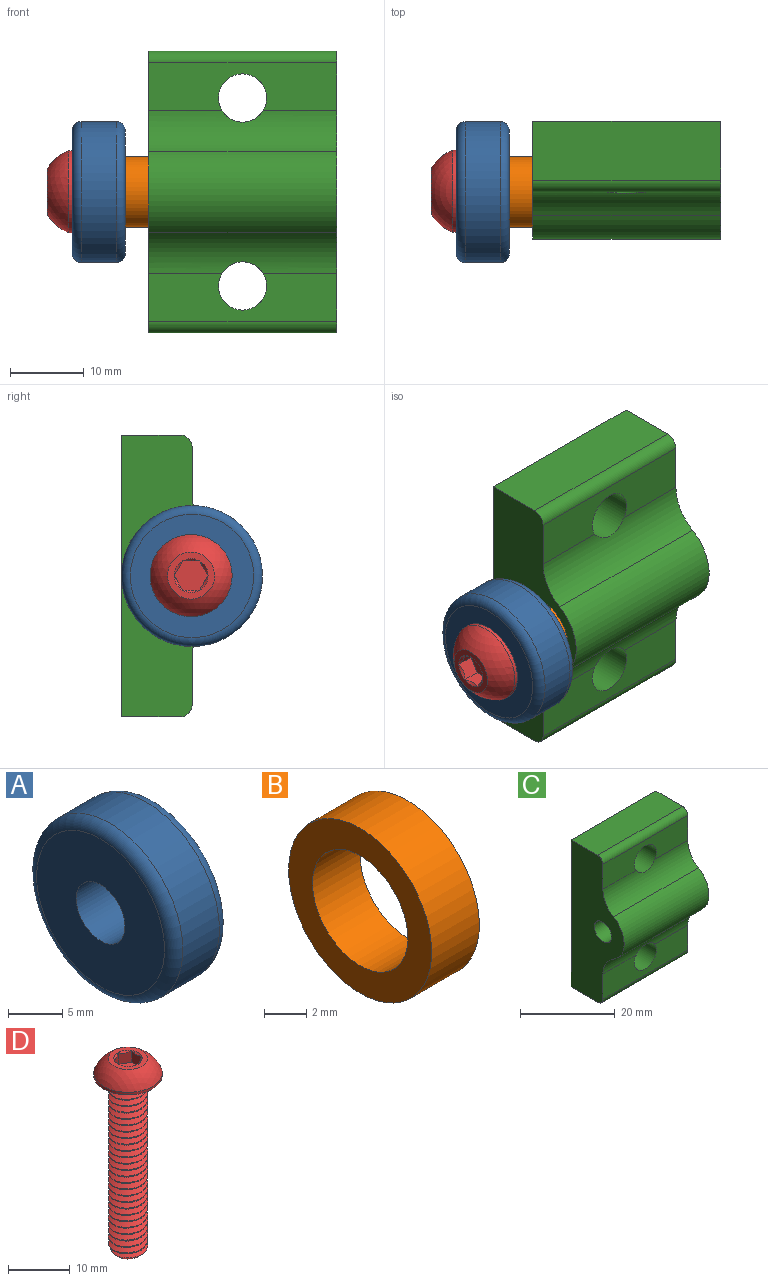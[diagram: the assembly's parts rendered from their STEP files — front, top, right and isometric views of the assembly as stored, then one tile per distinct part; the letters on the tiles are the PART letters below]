
ASSEMBLY  parts=4 mates=3
PART A: 6 faces, bbox 7.1x20.6x20.6 mm
  f0: cylinder r=3.17mm len=7.14mm, axis (-1,0,0), area 142.5mm2, adj f2,f3
  f1: cylinder r=9.53mm len=19.05mm, axis (-1,0,0), area 284.9mm2, adj f4,f5
  f2: plane 16.67x16.67mm, normal (1,0,0), area 186.6mm2, adj f0,f5
  f3: plane 16.67x16.67mm, normal (-1,0,0), area 186.6mm2, adj f0,f4
  f4: torus R=8.33mm, axis (1,0,0), area 106.8mm2, adj f1,f3
  f5: torus R=8.33mm, axis (1,0,0), area 106.8mm2, adj f1,f2
PART B: 4 faces, bbox 3.2x9.5x9.5 mm
  f0: cylinder r=3.17mm len=6.35mm, axis (-1,0,0), area 63.3mm2, adj f2,f3
  f1: cylinder r=4.76mm len=9.53mm, axis (-1,0,0), area 95mm2, adj f2,f3
  f2: plane 9.53x9.53mm, normal (1,0,0), area 39.6mm2, adj f0,f1
  f3: plane 9.53x9.53mm, normal (-1,0,0), area 39.6mm2, adj f0,f1
PART C: 15 faces, bbox 25.4x15.9x38.1 mm
  f0: cylinder r=6.35mm len=25.4mm, axis (-1,0,0), area 162.7mm2, adj f4,f5,f10,f11,f13
  f1: cylinder r=6.35mm len=25.4mm, axis (-1,0,0), area 162.7mm2, adj f3,f4,f10,f11,f12
  f2: cylinder r=1.59mm len=25.4mm, axis (-1,0,0), area 63.3mm2, adj f3,f9,f10,f11
  f3: plane 25.4x6.46mm, normal (0,-1,0), area 136.9mm2, adj f1,f2,f10,f11,f12
  f4: cylinder r=6.35mm len=25.4mm, axis (-1,0,0), area 337.8mm2, adj f0,f1,f10,f11
  f5: plane 25.4x6.46mm, normal (0,-1,0), area 136.9mm2, adj f0,f6,f10,f11,f13
  f6: cylinder r=1.59mm len=25.4mm, axis (-1,0,0), area 63.3mm2, adj f5,f7,f10,f11
  f7: plane 25.4x7.94mm, normal (0,0,-1), area 201.6mm2, adj f6,f8,f10,f11
  f8: plane 38.1x25.4mm, normal (0,1,0), area 900.8mm2, adj f7,f9,f10,f11,f12,f13
  f9: plane 25.4x7.94mm, normal (0,0,1), area 201.6mm2, adj f2,f8,f10,f11
  f10: plane 38.1x15.88mm, normal (1,0,0), area 411.2mm2, adj f0,f1,f2,f3,f4,f5,f6,f7
  f11: plane 38.1x15.88mm, normal (-1,0,0), area 411.2mm2, adj f0,f1,f2,f3,f4,f5,f6,f7
  f12: cylinder r=3.26mm len=9.72mm, axis (0,1,0), area 196mm2, adj f1,f3,f8
  f13: cylinder r=3.26mm len=9.72mm, axis (0,1,0), area 196mm2, adj f0,f5,f8
  f14: cylinder r=2.55mm len=25.4mm, axis (-1,0,0), area 407.4mm2, adj f10,f11
PART D: 23 faces, bbox 12x12x40.5 mm
  f0: cone r=2.29mm half-angle=45deg, axis (0,0,1), area 0.5mm2, adj f9,f17
  f1: cylinder r=5.55mm len=11.1mm, axis (0,0,1), area 17.5mm2, adj f2,f10
  f2: sphere r=5.97mm, area 107mm2, adj f1,f9
  f3: cone r=2.22mm half-angle=45deg, axis (0,0,1), area 12.3mm2, adj f4,f5,f6,f7,f8
  f4: cylinder r=3.17mm len=33.97mm, axis (0,0,-1), area 84.7mm2, adj f3,f6,f8,f10
  f5: plane 4.45x4.45mm, normal (0,0,-1), area 15.5mm2, adj f3
  f6: bspline ~35.27x6.35mm, area 447.6mm2, adj f3,f4,f7,f10
  f7: cylinder r=2.35mm len=34.8mm, axis (0,0,-1), area 64.1mm2, adj f3,f6,f8,f10
  f8: bspline ~35.88x6.35mm, area 448.2mm2, adj f3,f4,f7,f10
  f9: plane 7.1x7.1mm, normal (0,0,1), area 15.2mm2, adj f0,f2,f11,f12,f13,f14,f15
  f10: plane 11.58x11.58mm, normal (0,0,-1), area 72.5mm2, adj f1,f4,f6,f7,f8
  f11: cone r=2.29mm half-angle=45deg, axis (0,0,1), area 0mm2, adj f9,f18
  f12: cone r=2.29mm half-angle=45deg, axis (0,0,1), area 0mm2, adj f9,f19
  f13: cone r=2.29mm half-angle=45deg, axis (0,0,1), area 0mm2, adj f9,f20
  f14: cone r=2.29mm half-angle=45deg, axis (0,0,1), area 0mm2, adj f9,f21
  f15: cone r=2.29mm half-angle=45deg, axis (0,0,1), area 0mm2, adj f9,f22
  f16: plane 4.58x3.97mm, normal (0,0,1), area 13.6mm2, adj f17,f18,f19,f20,f21,f22
  f17: plane 2.57x2.51mm, normal (-1,0,0), area 4.9mm2, adj f0,f16,f18,f22
  f18: plane 3.22x2.85mm, normal (-0.5,-0.87,0), area 4.9mm2, adj f11,f16,f17,f19
  f19: plane 3.22x2.85mm, normal (0.5,-0.87,0), area 4.9mm2, adj f12,f16,f18,f20
  f20: plane 3.22x3.16mm, normal (1,0,0), area 4.9mm2, adj f13,f16,f19,f21
  f21: plane 3.22x2.85mm, normal (0.5,0.87,0), area 4.9mm2, adj f14,f16,f20,f22
  f22: plane 3.22x2.85mm, normal (-0.5,0.87,0), area 4.9mm2, adj f15,f16,f17,f21
PLACE A t=(-23.02,-9.53,0)mm
PLACE B t=(-15.88,-9.53,0)mm
PLACE C t=(-12.7,0,-19.05)mm
PLACE D rot(axis=(0.71,0,-0.71),180deg) t=(-26.37,-9.4,0.05)mm
MATE fastened D.f10 <-> A.f0  axis (1,0,0) through (-23.02,-9.52,0)mm
MATE fastened A.f0 <-> B.f0  axis (1,0,0) through (-15.88,-9.53,0)mm
MATE fastened B.f0 <-> C.f4  axis (1,0,0) through (-12.7,-9.53,0)mm
